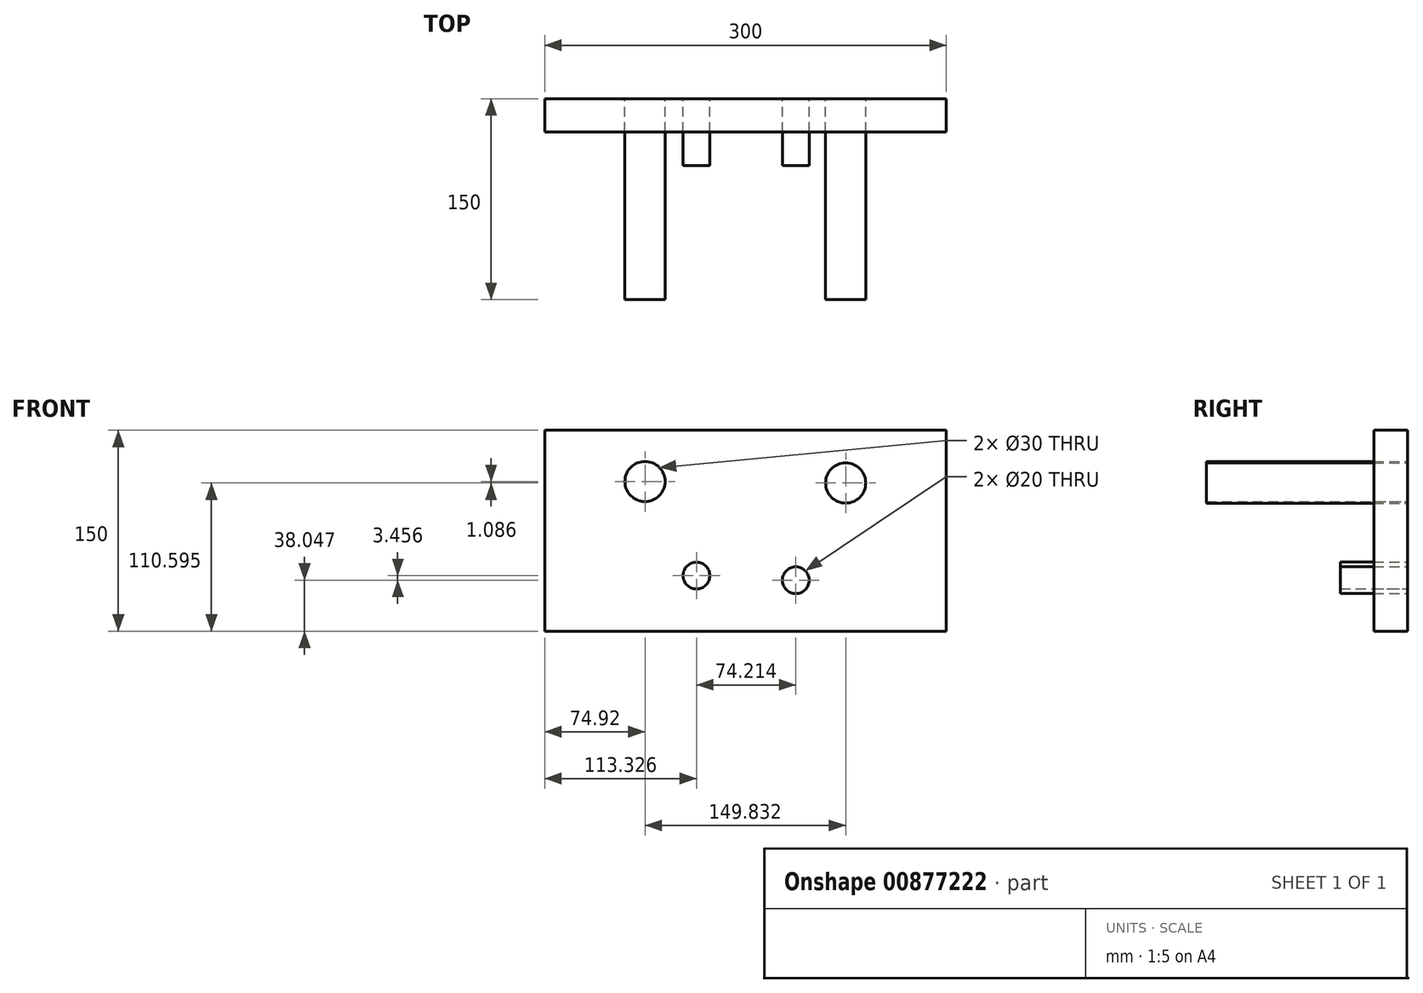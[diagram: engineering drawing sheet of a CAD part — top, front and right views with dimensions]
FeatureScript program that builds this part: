
annotation { "Feature Type Name" : "Feature", "Feature Type Description" : "" }
export const myFeature = defineFeature(function(context is Context, id is Id, definition is map)
    precondition{}
    {
        {
            var Q0;
            Q0=qCreatedBy(makeId("Front.planeOp"),FACE);
            var sketch = newSketch(context, id + "F0", { "sketchPlane" : qUnion([Q0])});
            skLineSegment(sketch, "E0.bottom", {"start": v(-150, -75) * mm, "end": v(150, -75) * mm});
            skLineSegment(sketch, "E0.top", {"start": v(-150, 75) * mm, "end": v(150, 75) * mm});
            skLineSegment(sketch, "E0.left", {"start": v(-150, -75) * mm, "end": v(-150, 75) * mm});
            skLineSegment(sketch, "E0.right", {"start": v(150, -75) * mm, "end": v(150, 75) * mm});
            skPoint(sketch, "E0.middle", {"position": v(0, 0) * mm});
            skCircle(sketch, "E1", {"center": v(-36.67, -33.5) * mm, "radius": 10 * mm});
            skCircle(sketch, "E2", {"center": v(37.54, -36.95) * mm, "radius": 10 * mm});
            skCircle(sketch, "E3", {"center": v(-75.08, 36.68) * mm, "radius": 15 * mm});
            skCircle(sketch, "E4", {"center": v(74.75, 35.6) * mm, "radius": 15 * mm});
            skSolve(sketch);
        }
        {
            var Q0;
            Q0=makeQuery(id+"F0.imprint","IMPRINT",FACE,{"disambiguationData":[TD([[makeQuery(id+"F0.imprint","IMPRINT",EDGE,{"derivedFrom":sQuery(id+"F0.wireOp",EDGE,"E4")}),1.0]])]});
            var Q1;
            Q1=makeQuery(id+"F0.imprint","IMPRINT",FACE,{"disambiguationData":[TD([[makeQuery(id+"F0.imprint","IMPRINT",EDGE,{"derivedFrom":sQuery(id+"F0.wireOp",EDGE,"E3")}),1.0]])]});
            extrude(context, id + "F1", {"entities" : qUnion([Q0, Q1]), "depth" : 150 * mm, "offsetDistance" : 25 * mm});
        }
        {
            var Q0;
            Q0=makeQuery(id+"F0.imprint","IMPRINT",FACE,{"disambiguationData":[TD([[makeQuery(id+"F0.imprint","IMPRINT",EDGE,{"derivedFrom":sQuery(id+"F0.wireOp",EDGE,"E2")}),1.0]])]});
            var Q1;
            Q1=makeQuery(id+"F0.imprint","IMPRINT",FACE,{"disambiguationData":[TD([[makeQuery(id+"F0.imprint","IMPRINT",EDGE,{"derivedFrom":sQuery(id+"F0.wireOp",EDGE,"E1")}),1.0]])]});
            extrude(context, id + "F2", {"entities" : qUnion([Q0, Q1]), "depth" : 50 * mm, "offsetDistance" : 25 * mm});
        }
        {
            var Q0;
            Q0=makeQuery(id+"F0.imprint","IMPRINT",FACE,{"disambiguationData":[TD([[makeQuery(id+"F0.imprint","IMPRINT",EDGE,{"derivedFrom":sQuery(id+"F0.wireOp",EDGE,"E0.bottom")}),1.0]])]});
            extrude(context, id + "F3", {"entities" : qUnion([Q0]), "depth" : 25 * mm, "offsetDistance" : 25 * mm});
        }
    });
